# Revit family: Furniture_Chair_YUMI_2
name_source: partatom
category: Furniture
units: mm (PartAtom-declared; Revit-internal decimal feet)

## family parameters
Always vertical = No
Cut with Voids When Loaded = No
OmniClass Number = 23.21.23.15.17
Room Calculation Point = No
Shared = No
Work Plane-Based = Yes

## types (3) — shared parameters
BIMobject category = Chair
BIMobject category code = furniture-chair
BIMobject main category = Furniture
BIMobject main category code = furniture
Brand url = https://www.sandlerseating.com
Default Elevation = 1219.2 mm  [stored 4 ft]
Description = Chair
Design country = UK
Edition number = 1
Frame = BS02 - YUMI
Heigth Shell = 450 mm  [stored 1.47638 ft]
IFC Classification = Furnishing Element
Manufacturer = Sandler
Manufacturer country = UK
Manufacturer name = Sandler
Masterformat 2014 Code = 12 48 43.13
Masterformat 2014 Description = Chair Mats
OmniClass Code = 23-21 23 15 17
Product Guid = ??
Product data url = https://www.sandlerseating.com
Product family = Furniture
Product group = Chair
Seat = TP01 - YUMI
Uniformat II Description = Movable Furnishings

## per-type parameters (varying)
| type | Frame Material | Seat Material | Shell Material | depth | height | width |
| YUMI 2.3 | Wood - Wenge Beech | Laminate - Grey | Laminate - Grey | 508.179 mm | 990.042 mm | 496.87 mm |
| YUMI 2.2 | Wood - Walnut Beech | Wood - Walnut Beech | Wood - Walnut Beech | 508.179 mm | 990.042 mm | 496.87 mm |
| YUMI 2.1 | Wood - Natural Beech | Leather - Tan - Sandler 131 | Leather - Tan - Sandler 131 | 560 mm  [stored 1.83727 ft] | 750 mm  [stored 2.46063 ft] | 590 mm  [stored 1.9357 ft] |

note: column(s) folded — value = type name in every type: Model, Product name

note: [stored X ft] marks values corroborated as IEEE doubles in the binary element streams (Revit-internal decimal feet)

## geometry (parser evidence)
native form markers: Sweep x7
no freeform markers — native parametric forms only
